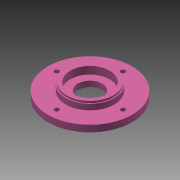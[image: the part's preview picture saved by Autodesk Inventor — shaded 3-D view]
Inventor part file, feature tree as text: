
AUTODESK INVENTOR PART (.ipt)
format: ipt  version: 2015 (Build 190159000, 159)  size: 152,064 bytes
history: native  units: mm
features: extrude x6, sketch x6, fillet x1
ambient origin geometry x8: Origin, YZ Plane, XZ Plane, XY Plane, X Axis, Y Axis, Z Axis, Center Point
bodies: 实体1 (feature_tree)
feature tree (13):
  extrude  "拉伸1"  Depth=7.0mm TaperAngle=0.0deg
  extrude  "拉伸2"  Depth=42.0mm
  extrude  "拉伸3"  Depth=8.0mm
  extrude  "拉伸4"  Depth=2.0mm TaperAngle=0.0deg
  extrude  "拉伸5"  Depth=26.0mm
  extrude  "拉伸6"  Depth=0.5mm
  fillet  "圆角1"  Radius=5.0mm
  sketch  "草图1"  dims[d0=90.0mm d1=7.0mm d2=0.0mm]
  sketch  "草图2"  dims[d3=52.0mm d4=42.0mm]
  sketch  "草图3"  dims[d5=8.0mm d6=0.0mm d7=52.0mm]
  sketch  "草图4"  dims[d8=50.0mm d9=2.0mm d10=0.0mm]
  sketch  "草图5"  dims[d11=26.0mm d12=26.0mm]
  sketch  "草图6"  dims[d13=0.0mm d15=5.0mm d16=5.0mm d17=5.0mm d18=5.0mm d19=35.5mm d20=35.5mm d21=35.5mm d22=35.5mm d23=7.266692mm d24=3.861367mm d25=8.0mm d26=0.0mm d27=45.0mm d28=1.0mm d29=0.0mm d30=0.5mm]
